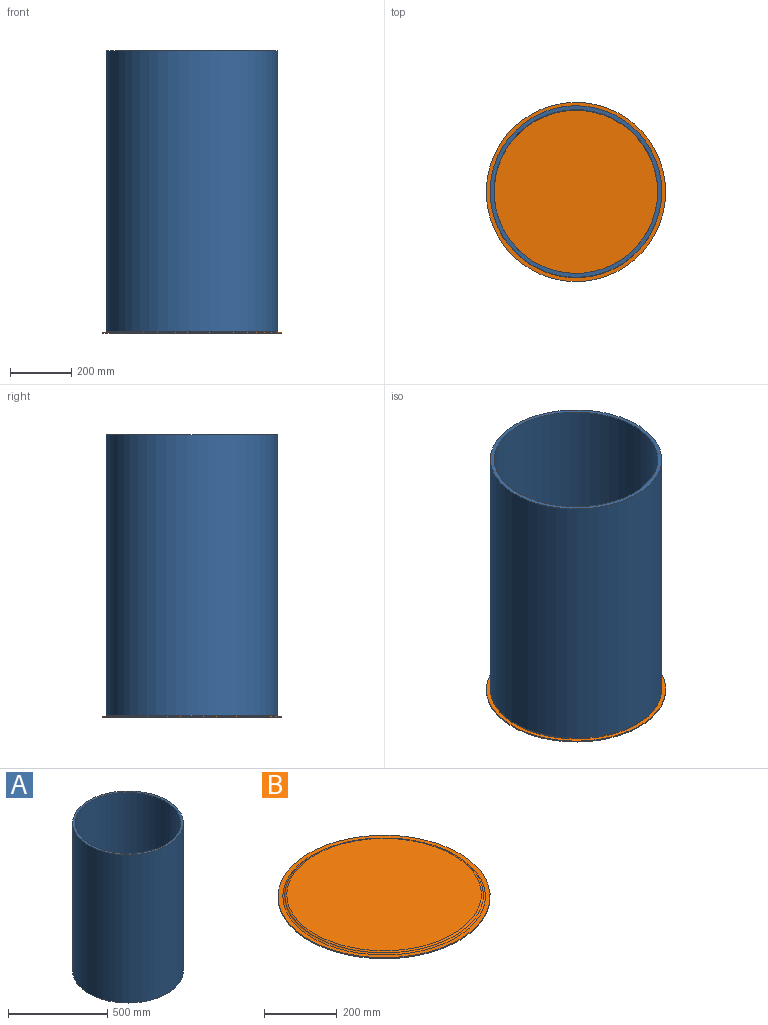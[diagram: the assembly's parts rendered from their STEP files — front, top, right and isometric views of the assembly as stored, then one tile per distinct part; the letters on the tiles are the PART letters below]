
ASSEMBLY  parts=2 mates=1
PART A: 4 faces, bbox 558.8x558.8x914.4 mm
  f0: cylinder r=266.7mm len=914.4mm, axis (0,0,-1), area 1532283.4mm2, adj f2,f3
  f1: cylinder r=279.4mm len=914.4mm, axis (0,0,-1), area 1605249.3mm2, adj f2,f3
  f2: plane 558.8x558.8mm, normal (0,0,1), area 21788.4mm2, adj f0,f1
  f3: plane 558.8x558.8mm, normal (0,0,-1), area 21788.4mm2, adj f0,f1
PART B: 9 faces, bbox 618.9x618.9x9.8 mm
  f0: torus R=278.96mm, axis (0,0,1), area 15522.2mm2, adj f1,f8
  f1: plane 584.2x584.2mm, normal (0,0,-1), area 23572mm2, adj f0,f2
  f2: cylinder r=292.1mm len=584.2mm, axis (0,0,1), area 6293.3mm2, adj f1,f3
  f3: plane 584.2x584.2mm, normal (0,0,1), area 23572mm2, adj f2,f4
  f4: torus R=278.96mm, axis (0,0,1), area 11528.7mm2, adj f3,f5
  f5: torus R=267.96mm, axis (0,0,1), area 11322.5mm2, adj f4,f6
  f6: plane 535.93x535.93mm, normal (0,0,1), area 225578.5mm2, adj f5
  f7: plane 532.27x532.27mm, normal (0,0,-1), area 222511.5mm2, adj f8
  f8: torus R=266.13mm, axis (0,0,1), area 9862.2mm2, adj f0,f7
PLACE A t=(0,0,2.92)mm
PLACE B t=(0,0,6.35)mm
MATE fastened B.f0 <-> A.f0  axis (0,0,-1) through (0,0,2.92)mm
